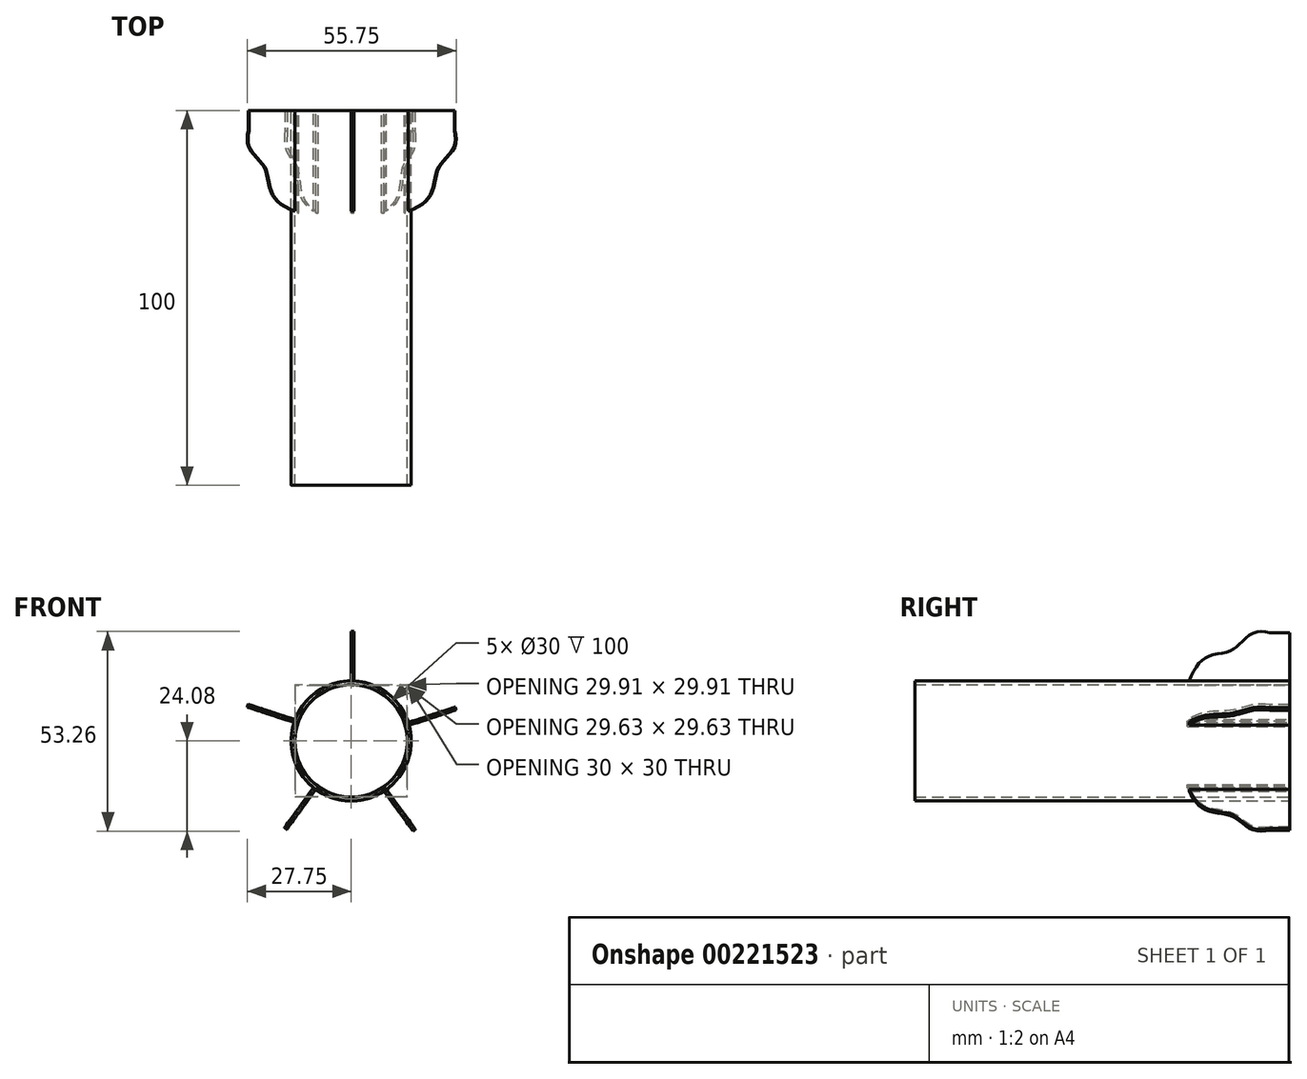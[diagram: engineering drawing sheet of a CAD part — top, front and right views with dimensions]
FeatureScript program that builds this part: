
annotation { "Feature Type Name" : "Feature", "Feature Type Description" : "" }
export const myFeature = defineFeature(function(context is Context, id is Id, definition is map)
    precondition{}
    {
        {
            var Q0;
            Q0=qCreatedBy(makeId("Front.planeOp"),FACE);
            var sketch = newSketch(context, id + "F0", { "sketchPlane" : qUnion([Q0])});
            skCircle(sketch, "E0", {"center": v(0, 0) * mm, "radius": 15 * mm});
            skCircle(sketch, "E1", {"center": v(0, 0) * mm, "radius": 16 * mm});
            skSolve(sketch);
        }
        {
            var Q0;
            Q0=makeQuery(id+"F0.imprint","IMPRINT",FACE,{"disambiguationData":[TD([[makeQuery(id+"F0.imprint","IMPRINT",EDGE,{"derivedFrom":sQuery(id+"F0.wireOp",EDGE,"E0")}),-1.0]])]});
            extrude(context, id + "F1", {"entities" : qUnion([Q0]), "depth" : 100 * mm});
        }
        {
            var Q0;
            Q0=qCreatedBy(makeId("Right.planeOp"),FACE);
            var sketch = newSketch(context, id + "F2", { "sketchPlane" : qUnion([Q0])});
            skLineSegment(sketch, "E2", {"start": v(-27.3, 14.93) * mm, "end": v(0, 14.93) * mm});
            skLineSegment(sketch, "E3", {"start": v(0, 14.93) * mm, "end": v(0, 28.9) * mm});
            skLineSegment(sketch, "E4", {"start": v(0, 28.9) * mm, "end": v(-5.38, 28.9) * mm});
            skFitSpline(sketch, "E5", {"points": [v(-5.38, 28.9) * mm, v(-9.49, 28.9) * mm, v(-13.32, 25.88) * mm, v(-16.06, 23.97) * mm, v(-20.72, 22.87) * mm, v(-24.28, 20.68) * mm, v(-27.3, 14.93) * mm], "startDerivative": vector(-26.6, 4.7) * mm, "endDerivative": vector(-13.65, -32.8) * mm});
            skSolve(sketch);
        }
        {
            var Q0;
            Q0=makeQuery(id+"F2.imprint","IMPRINT",FACE,{"disambiguationData":[TD([[makeQuery(id+"F2.imprint","IMPRINT",EDGE,{"derivedFrom":sQuery(id+"F2.wireOp",EDGE,"E2")}),1.0]])]});
            extrude(context, id + "F3", {"entities" : qUnion([Q0]), "operationType" : NewBodyOperationType.ADD, "depth" : 0.8 * mm});
        }
        {
            var Q0;
            Q0=makeQuery(id+"F1.opExtrude","SWEPT_BODY",BODY,{"disambiguationData":[OSD([sQuery(id+"F0.wireOp",EDGE,"E0"),sQuery(id+"F0.wireOp",EDGE,"E1")])]});
            var Q1;
            Q1=makeQuery(id+"F1.opExtrude","SWEPT_FACE",FACE,{"disambiguationData":[OSD([sQuery(id+"F0.wireOp",EDGE,"E1")])]});
            circularPattern(context, id + "F4", {"entities" : qUnion([Q0]), "axis" : qUnion([Q1]), "angle" : 360 * degree, "instanceCount" : 5, "equalSpace" : true});
        }
    });
